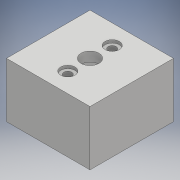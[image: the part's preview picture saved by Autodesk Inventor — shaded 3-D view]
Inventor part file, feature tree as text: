
AUTODESK INVENTOR PART (.ipt)
format: ipt  version: 2018.2 (Build 222227000, 227)  size: 126,976 bytes
history: native  units: mm
features: extrude x3, sketch x3
ambient origin geometry x8: Origin, YZ Plane, XZ Plane, XY Plane, X Axis, Y Axis, Z Axis, Center Point
bodies: Solid1 (feature_tree)
feature tree (6):
  extrude  "Extrusion1"  Depth=35.0mm
  extrude  "Extrusion2"  Depth=19.0mm TaperAngle=0.0deg
  extrude  "Extrusion3"  Depth=1.2mm
  sketch  "Sketch1"  dims[d0=35.0mm d1=35.0mm]
  sketch  "Sketch2"  dims[d2=25.5mm d3=19.0mm d4=0.0mm]
  sketch  "Sketch3"  dims[d5=7.5mm d6=17.5mm d7=17.5mm d8=3.3mm d9=3.3mm d10=9.3mm d11=9.3mm d12=4.0mm d13=0.0mm d14=6.0mm d15=6.0mm d16=1.2mm d17=0.0mm]
